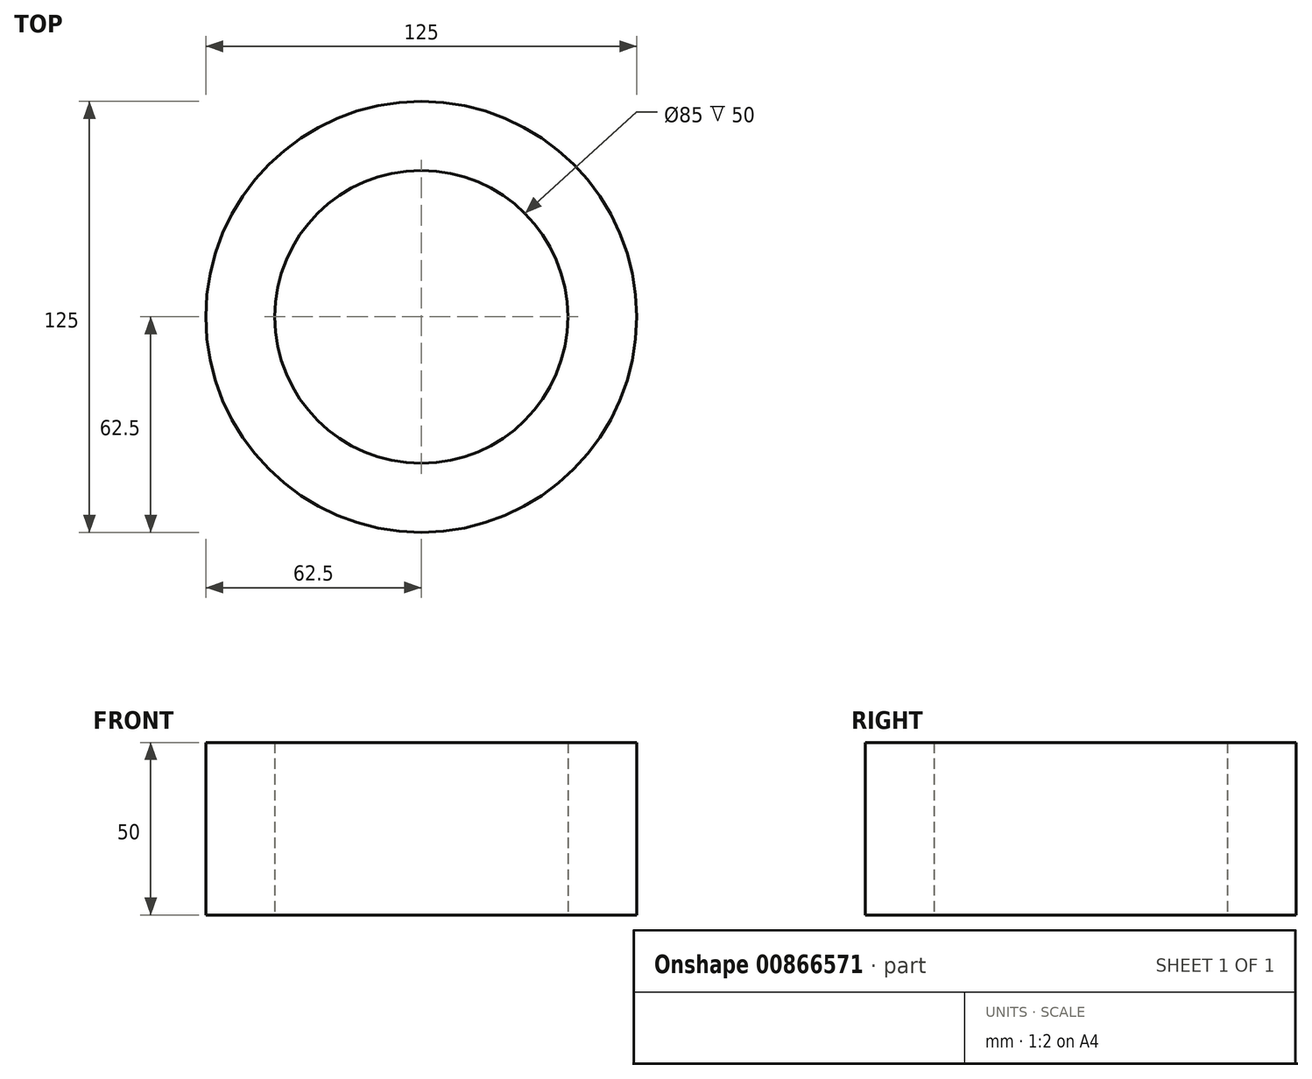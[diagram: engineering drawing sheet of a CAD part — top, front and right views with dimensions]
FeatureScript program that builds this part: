
annotation { "Feature Type Name" : "Feature", "Feature Type Description" : "" }
export const myFeature = defineFeature(function(context is Context, id is Id, definition is map)
    precondition{}
    {
        {
            var Q0;
            Q0=qCreatedBy(makeId("Top.planeOp"),FACE);
            var sketch = newSketch(context, id + "F0", { "sketchPlane" : qUnion([Q0])});
            skCircle(sketch, "E0", {"center": v(0, 0) * mm, "radius": 62.5 * mm});
            skCircle(sketch, "E1", {"center": v(0, 0) * mm, "radius": 42.5 * mm});
            skSolve(sketch);
        }
        {
            var Q0;
            Q0=makeQuery(id+"F0.imprint","IMPRINT",FACE,{"disambiguationData":[TD([[makeQuery(id+"F0.imprint","IMPRINT",EDGE,{"derivedFrom":sQuery(id+"F0.wireOp",EDGE,"E0")}),1.0]])]});
            extrude(context, id + "F1", {"entities" : qUnion([Q0]), "depth" : 25 * mm, "offsetDistance" : 25 * mm, "hasSecondDirection" : true, "secondDirectionOppositeDirection" : true, "secondDirectionDepth" : 25 * mm});
        }
    });
